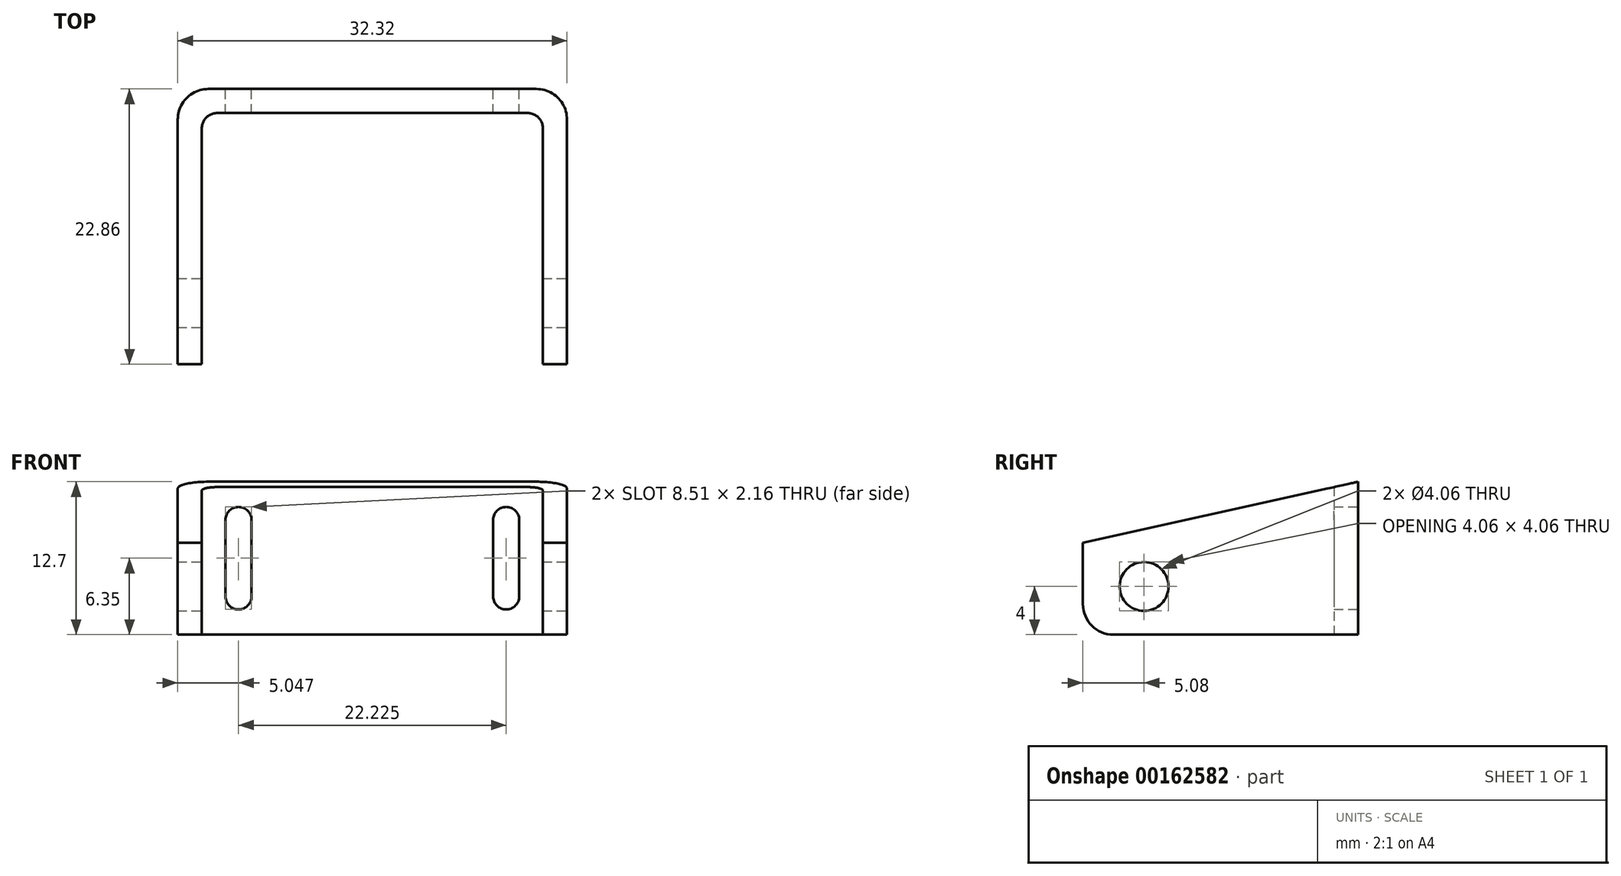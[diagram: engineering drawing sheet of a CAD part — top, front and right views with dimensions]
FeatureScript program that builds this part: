
annotation { "Feature Type Name" : "Feature", "Feature Type Description" : "" }
export const myFeature = defineFeature(function(context is Context, id is Id, definition is map)
    precondition{}
    {
        {
            var Q0;
            Q0=qCreatedBy(makeId("Top.planeOp"),FACE);
            var sketch = newSketch(context, id + "F0", { "sketchPlane" : qUnion([Q0])});
            skLineSegment(sketch, "E0", {"start": v(0, 0) * mm, "end": v(0, -30.52) * mm, "construction": true});
            skLineSegment(sketch, "E1", {"start": v(0, 0) * mm, "end": v(13.62, 0) * mm});
            skLineSegment(sketch, "E2", {"start": v(16.16, -2.54) * mm, "end": v(16.16, -22.86) * mm});
            skLineSegment(sketch, "E3", {"start": v(16.16, -22.86) * mm, "end": v(14.16, -22.86) * mm});
            skLineSegment(sketch, "E4", {"start": v(14.16, -22.86) * mm, "end": v(14.16, -3.27) * mm});
            skLineSegment(sketch, "E5", {"start": v(12.9, -2) * mm, "end": v(0, -2) * mm});
            skLineSegment(sketch, "E6.MirrorCS", {"start": v(-16.16, -22.86) * mm, "end": v(-14.16, -22.86) * mm});
            skLineSegment(sketch, "E7.MirrorCS", {"start": v(-12.9, -2) * mm, "end": v(0, -2) * mm});
            skLineSegment(sketch, "E8.MirrorCS", {"start": v(-14.16, -22.86) * mm, "end": v(-14.16, -3.27) * mm});
            skLineSegment(sketch, "E9.MirrorCS", {"start": v(-16.16, -2.54) * mm, "end": v(-16.16, -22.86) * mm});
            skLineSegment(sketch, "E10.MirrorCS", {"start": v(0, 0) * mm, "end": v(-13.62, 0) * mm});
            skPoint(sketch, "E11.orphan", {"position": v(-16.16, 0) * mm});
            skPoint(sketch, "E12.orphan", {"position": v(16.16, 0) * mm});
            skPoint(sketch, "E13.visualSharp", {"position": v(-14.16, -2) * mm});
            skArc(sketch, "E13.filletArc", {"start": v(-12.9, -2) * mm, "mid": v(-13.79, -2.37) * mm, "end": v(-14.16, -3.27) * mm});
            skPoint(sketch, "E14.visualSharp", {"position": v(14.16, -2) * mm});
            skArc(sketch, "E14.filletArc", {"start": v(14.16, -3.27) * mm, "mid": v(13.79, -2.37) * mm, "end": v(12.9, -2) * mm});
            skArc(sketch, "E15.filletArc", {"start": v(-13.62, 0) * mm, "mid": v(-15.42, -0.74) * mm, "end": v(-16.16, -2.54) * mm});
            skArc(sketch, "E16.filletArc", {"start": v(16.16, -2.54) * mm, "mid": v(15.42, -0.74) * mm, "end": v(13.62, 0) * mm});
            skSolve(sketch);
        }
        {
            var Q0;
            Q0 = qSketchRegion(id + "F0", true);
            extrude(context, id + "F1", {"entities" : qUnion([Q0]), "depth" : 12.7 * mm});
        }
        {
            var Q0;
            Q0=qCreatedBy(makeId("Right.planeOp"),FACE);
            var sketch = newSketch(context, id + "F2", { "sketchPlane" : qUnion([Q0])});
            skLineSegment(sketch, "E17.0", {"start": v(-2.54, 12.7) * mm, "end": v(-22.86, 12.7) * mm});
            skLineSegment(sketch, "E18.0", {"start": v(-2.54, 12.7) * mm, "end": v(0, 12.7) * mm});
            skLineSegment(sketch, "E19.0", {"start": v(-22.86, 12.7) * mm, "end": v(-22.86, 7.62) * mm});
            skLineSegment(sketch, "E20", {"start": v(0, 12.7) * mm, "end": v(-22.86, 7.62) * mm});
            skPoint(sketch, "E21.orphan", {"position": v(-22.86, 0) * mm});
            skSolve(sketch);
        }
        {
            var Q0;
            Q0 = qSketchRegion(id + "F2", true);
            extrude(context, id + "F3", {"entities" : qUnion([Q0]), "operationType" : NewBodyOperationType.REMOVE, "endBound" : BoundingType.THROUGH_ALL, "oppositeDirection" : true, "depth" : 25.4 * mm, "hasSecondDirection" : true, "secondDirectionBound" : SecondDirectionBoundingType.THROUGH_ALL, "secondDirectionOppositeDirection" : false, "secondDirectionDepth" : 25.4 * mm});
        }
        {
            var Q0;
            Q0=makeQuery(id+"F1.opExtrude","SWEPT_FACE",FACE,{"disambiguationData":[OSD([sQuery(id+"F0.wireOp",EDGE,"E2")])]});
            var sketch = newSketch(context, id + "F4", { "sketchPlane" : qUnion([Q0])});
            skCircle(sketch, "E22", {"center": v(-17.78, 4) * mm, "radius": 2.03 * mm});
            skSolve(sketch);
        }
        {
            var Q0;
            Q0 = qSketchRegion(id + "F4", true);
            var Q1;
            Q1 = qSketchRegion(id + "F7", true);
            extrude(context, id + "F5", {"entities" : qUnion([Q0, Q1]), "operationType" : NewBodyOperationType.REMOVE, "endBound" : BoundingType.THROUGH_ALL, "oppositeDirection" : true, "depth" : 25.4 * mm, "hasSecondDirection" : true, "secondDirectionBound" : SecondDirectionBoundingType.THROUGH_ALL, "secondDirectionOppositeDirection" : false, "secondDirectionDepth" : 25.4 * mm});
        }
        {
            var Q0;
            {var subQ0=sQuery(id+"F2.wireOp",EDGE,"E20");Q0=makeQuery(id+"F3.boolean.opBoolean","COPY",EDGE,{"disambiguationData":[TD([makeQuery(id+"F1.opExtrude","SWEPT_FACE",FACE,{"disambiguationData":[OSD([sQuery(id+"F0.wireOp",EDGE,"E2")])]})])],"derivedFrom":makeQuery(id+"F3.opExtrude","SWEPT_EDGE",EDGE,{"disambiguationData":[OSD([sQuery(id+"F2.wireOp",EDGE,"E19.0"),subQ0])]})});}
            var Q1;
            {var subQ0=sQuery(id+"F2.wireOp",EDGE,"E20");Q1=makeQuery(id+"F3.boolean.opBoolean","COPY",EDGE,{"disambiguationData":[TD([makeQuery(id+"F1.opExtrude","SWEPT_FACE",FACE,{"disambiguationData":[OSD([sQuery(id+"F0.wireOp",EDGE,"E6.MirrorCS")])]})])],"derivedFrom":makeQuery(id+"F3.opExtrude","SWEPT_EDGE",EDGE,{"disambiguationData":[OSD([sQuery(id+"F2.wireOp",EDGE,"E19.0"),subQ0])]})});}
            var Q2;
            Q2=makeQuery(id+"F1.opExtrude","CAP_EDGE",EDGE,{"disambiguationData":[OSD([sQuery(id+"F0.wireOp",EDGE,"E6.MirrorCS")])],"isStart":true});
            var Q3;
            Q3=makeQuery(id+"F1.opExtrude","CAP_EDGE",EDGE,{"disambiguationData":[OSD([sQuery(id+"F0.wireOp",EDGE,"E3")])],"isStart":true});
            fillet(context, id + "F6", {"entities" : qUnion([Q0, Q1, Q2, Q3]), "radius" : 2.54 * mm, "tangentPropagation" : true, "allowEdgeOverflow" : false});
        }
        {
            var Q0;
            Q0=makeQuery(id+"F1.opExtrude","SWEPT_FACE",FACE,{"disambiguationData":[OSD([sQuery(id+"F0.wireOp",EDGE,"E1"),sQuery(id+"F0.wireOp",EDGE,"E10.MirrorCS")])]});
            var sketch = newSketch(context, id + "F7", { "sketchPlane" : qUnion([Q0])});
            skLineSegment(sketch, "E23", {"start": v(0, 0) * mm, "end": v(0, 17.76) * mm, "construction": true});
            skPoint(sketch, "E23.endSnap0", {"position": v(0, 12.7) * mm});
            skLineSegment(sketch, "E24", {"start": v(-11.11, 12.7) * mm, "end": v(-11.11, 0) * mm, "construction": true});
            skArc(sketch, "E25", {"start": v(-10.03, 9.53) * mm, "mid": v(-11.11, 10.6) * mm, "end": v(-12.2, 9.53) * mm});
            skArc(sketch, "E26", {"start": v(-12.2, 3.18) * mm, "mid": v(-11.11, 2.1) * mm, "end": v(-10.03, 3.18) * mm});
            skLineSegment(sketch, "E27", {"start": v(-10.03, 9.53) * mm, "end": v(-10.03, 3.18) * mm});
            skLineSegment(sketch, "E28", {"start": v(-12.2, 3.18) * mm, "end": v(-12.2, 9.53) * mm});
            skLineSegment(sketch, "E29.MirrorCS", {"start": v(11.11, 12.7) * mm, "end": v(11.11, 0) * mm, "construction": true});
            skArc(sketch, "E30.MirrorCS", {"start": v(12.2, 3.18) * mm, "mid": v(11.11, 2.1) * mm, "end": v(10.03, 3.18) * mm});
            skLineSegment(sketch, "E31.MirrorCS", {"start": v(10.03, 9.53) * mm, "end": v(10.03, 3.18) * mm});
            skLineSegment(sketch, "E32.MirrorCS", {"start": v(12.2, 3.18) * mm, "end": v(12.2, 9.53) * mm});
            skArc(sketch, "E33.MirrorCS", {"start": v(10.03, 9.53) * mm, "mid": v(11.11, 10.6) * mm, "end": v(12.2, 9.53) * mm});
            skSolve(sketch);
        }
        {
            var Q0;
            Q0 = qSketchRegion(id + "F7", true);
            extrude(context, id + "F8", {"entities" : qUnion([Q0]), "operationType" : NewBodyOperationType.REMOVE, "endBound" : BoundingType.THROUGH_ALL, "oppositeDirection" : true, "depth" : 25.4 * mm});
        }
    });
